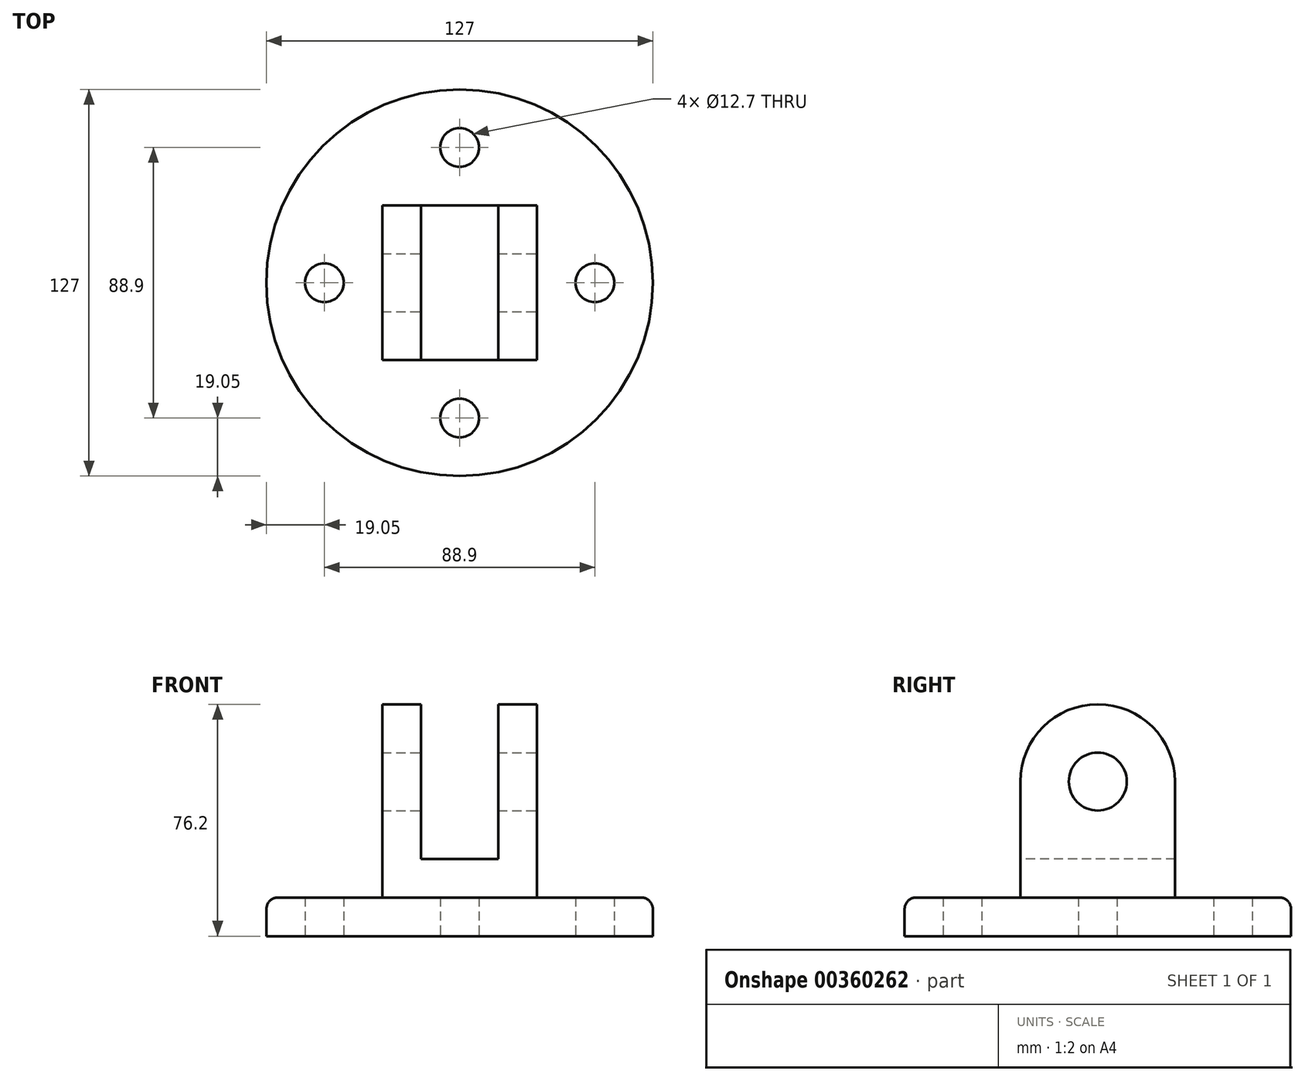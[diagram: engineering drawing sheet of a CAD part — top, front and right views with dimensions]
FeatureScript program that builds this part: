
annotation { "Feature Type Name" : "Feature", "Feature Type Description" : "" }
export const myFeature = defineFeature(function(context is Context, id is Id, definition is map)
    precondition{}
    {
        {
            var Q0;
            Q0=qCreatedBy(makeId("Top.planeOp"),FACE);
            var sketch = newSketch(context, id + "F0", { "sketchPlane" : qUnion([Q0])});
            skCircle(sketch, "E0", {"center": v(0, 0) * mm, "radius": 63.5 * mm});
            skCircle(sketch, "E1", {"center": v(0, 44.45) * mm, "radius": 6.35 * mm});
            skCircle(sketch, "E2.1.0", {"center": v(44.45, 0) * mm, "radius": 6.35 * mm});
            skCircle(sketch, "E2.2.0", {"center": v(0, -44.45) * mm, "radius": 6.35 * mm});
            skCircle(sketch, "E2.3.0", {"center": v(-44.45, 0) * mm, "radius": 6.35 * mm});
            skLineSegment(sketch, "E2.anchor1", {"start": v(0, 0) * mm, "end": v(0, 44.45) * mm, "construction": true});
            skLineSegment(sketch, "E2.anchor2", {"start": v(0, 0) * mm, "end": v(-44.45, 0) * mm, "construction": true});
            skSolve(sketch);
        }
        {
            var Q0;
            Q0=makeQuery(id+"F0.imprint","IMPRINT",FACE,{"disambiguationData":[TD([[makeQuery(id+"F0.imprint","IMPRINT",EDGE,{"derivedFrom":sQuery(id+"F0.wireOp",EDGE,"E0")}),1.0]])]});
            extrude(context, id + "F1", {"entities" : qUnion([Q0]), "endBound" : BoundingType.SYMMETRIC, "depth" : 12.7 * mm});
        }
        {
            var Q0;
            Q0=makeQuery(id+"F1.opExtrude","CAP_FACE",FACE,{"disambiguationData":[OSD([sQuery(id+"F0.wireOp",EDGE,"E0"),sQuery(id+"F0.wireOp",EDGE,"E1"),sQuery(id+"F0.wireOp",EDGE,"E2.1.0"),sQuery(id+"F0.wireOp",EDGE,"E2.2.0"),sQuery(id+"F0.wireOp",EDGE,"E2.3.0")])],"isStart":false});
            var sketch = newSketch(context, id + "F2", { "sketchPlane" : qUnion([Q0])});
            skLineSegment(sketch, "E3.bottom", {"start": v(25.4, -25.4) * mm, "end": v(-25.4, -25.4) * mm});
            skLineSegment(sketch, "E3.top", {"start": v(25.4, 25.4) * mm, "end": v(-25.4, 25.4) * mm});
            skLineSegment(sketch, "E3.left", {"start": v(25.4, -25.4) * mm, "end": v(25.4, 25.4) * mm});
            skLineSegment(sketch, "E3.right", {"start": v(-25.4, -25.4) * mm, "end": v(-25.4, 25.4) * mm});
            skPoint(sketch, "E3.middle", {"position": v(0, 0) * mm});
            skSolve(sketch);
        }
        {
            var Q0;
            Q0=makeQuery(id+"F2.imprint","IMPRINT",FACE,{"disambiguationData":[TD([[makeQuery(id+"F2.imprint","IMPRINT",EDGE,{"derivedFrom":sQuery(id+"F2.wireOp",EDGE,"E3.bottom")}),-1.0]])]});
            extrude(context, id + "F3", {"entities" : qUnion([Q0]), "operationType" : NewBodyOperationType.ADD, "depth" : 38.1 * mm});
        }
        {
            var Q0;
            Q0=makeQuery(id+"F3.opExtrude","SWEPT_FACE",FACE,{"disambiguationData":[OSD([sQuery(id+"F2.wireOp",EDGE,"E3.left")])]});
            var sketch = newSketch(context, id + "F4", { "sketchPlane" : qUnion([Q0])});
            skArc(sketch, "E4", {"start": v(25.4, 44.45) * mm, "mid": v(0, 69.85) * mm, "end": v(-25.4, 44.45) * mm});
            skSolve(sketch);
        }
        {
            var Q0;
            Q0=makeQuery(id+"F4.imprint","IMPRINT",FACE,{"disambiguationData":[TD([[makeQuery(id+"F4.imprint","IMPRINT",EDGE,{"derivedFrom":sQuery(id+"F4.wireOp",EDGE,"E4")}),1.0]])]});
            var Q1;
            Q1=makeQuery(id+"F3.opExtrude","SWEPT_FACE",FACE,{"disambiguationData":[OSD([sQuery(id+"F2.wireOp",EDGE,"E3.right")])]});
            extrude(context, id + "F5", {"entities" : qUnion([Q0]), "operationType" : NewBodyOperationType.ADD, "endBound" : BoundingType.UP_TO_SURFACE, "oppositeDirection" : true, "endBoundEntityFace" : qUnion([Q1]), "depth" : 25.4 * mm});
        }
        {
            var Q0;
            Q0=makeQuery(id+"F3.opExtrude","SWEPT_FACE",FACE,{"disambiguationData":[OSD([sQuery(id+"F2.wireOp",EDGE,"E3.bottom")])]});
            var sketch = newSketch(context, id + "F6", { "sketchPlane" : qUnion([Q0])});
            skLineSegment(sketch, "E5.bottom", {"start": v(-12.7, 69.85) * mm, "end": v(12.7, 69.85) * mm});
            skLineSegment(sketch, "E5.top", {"start": v(-12.7, 19.05) * mm, "end": v(12.7, 19.05) * mm});
            skLineSegment(sketch, "E5.left", {"start": v(-12.7, 69.85) * mm, "end": v(-12.7, 19.05) * mm});
            skLineSegment(sketch, "E5.right", {"start": v(12.7, 69.85) * mm, "end": v(12.7, 19.05) * mm});
            skLineSegment(sketch, "E6", {"start": v(0, 0) * mm, "end": v(0, 73.44) * mm, "construction": true});
            skPoint(sketch, "E6.endSnap0", {"position": v(0, 6.35) * mm});
            skLineSegment(sketch, "E7", {"start": v(-25.4, 69.85) * mm, "end": v(25.4, 69.85) * mm});
            skSolve(sketch);
        }
        {
            var Q0;
            {var subQ0=sQuery(id+"F6.wireOp",EDGE,"E5.top");Q0=makeQuery(id+"F6.imprint","IMPRINT",FACE,{"disambiguationData":[TD([[makeQuery(id+"F6.imprint","IMPRINT",EDGE,{"derivedFrom":subQ0}),1.0]])]});}
            var Q1;
            {var subQ0=sQuery(id+"F6.wireOp",EDGE,"E5.bottom");Q1=makeQuery(id+"F6.imprint","IMPRINT",FACE,{"disambiguationData":[TD([[makeQuery(id+"F6.imprint","IMPRINT",EDGE,{"derivedFrom":subQ0}),-1.0]])]});}
            var Q2;
            {var subQ0=sQuery(id+"F6.wireOp",EDGE,"E7");var subQ1=sQuery(id+"F6.wireOp",EDGE,"E5.left");var subQ2=makeQuery(id+"F6.imprint","INTERSECT",VERTEX,{"derivedFrom":[subQ1,subQ0]});Q2=makeQuery(id+"F6.imprint","IMPRINT",FACE,{"disambiguationData":[TD([[makeQuery(id+"F6.imprint","IMPRINT",EDGE,{"disambiguationData":[TD([[subQ2,-1.0]])],"derivedFrom":subQ0}),-1.0]])]});}
            extrude(context, id + "F7", {"entities" : qUnion([Q0, Q1, Q2]), "operationType" : NewBodyOperationType.REMOVE, "endBound" : BoundingType.THROUGH_ALL, "oppositeDirection" : true, "depth" : 25.4 * mm});
        }
        {
            var Q0;
            {var subQ0=sQuery(id+"F2.wireOp",EDGE,"E3.left");Q0=makeQuery(id+"F5.boolean.opBoolean","MERGE",FACE,{"derivedFrom":[makeQuery(id+"F3.opExtrude","SWEPT_FACE",FACE,{"disambiguationData":[OSD([subQ0])]}),makeQuery(id+"F5.opExtrude","CAP_FACE",FACE,{"disambiguationData":[OSD([subQ0,sQuery(id+"F4.wireOp",EDGE,"E4")])],"isStart":true})]});}
            var sketch = newSketch(context, id + "F8", { "sketchPlane" : qUnion([Q0])});
            skCircle(sketch, "E8", {"center": v(0, 44.45) * mm, "radius": 9.53 * mm});
            skSolve(sketch);
        }
        {
            var Q0;
            Q0=makeQuery(id+"F8.imprint","IMPRINT",FACE,{"disambiguationData":[TD([[makeQuery(id+"F8.imprint","IMPRINT",EDGE,{"derivedFrom":sQuery(id+"F8.wireOp",EDGE,"E8")}),1.0]])]});
            extrude(context, id + "F9", {"entities" : qUnion([Q0]), "operationType" : NewBodyOperationType.REMOVE, "endBound" : BoundingType.THROUGH_ALL, "oppositeDirection" : true, "depth" : 25.4 * mm});
        }
        {
            var Q0;
            Q0=makeQuery(id+"F1.opExtrude","CAP_EDGE",EDGE,{"disambiguationData":[OSD([sQuery(id+"F0.wireOp",EDGE,"E0")])],"isStart":false});
            var Q1;
            Q1=makeQuery(id+"F3.opExtrude","CAP_EDGE",EDGE,{"disambiguationData":[OSD([sQuery(id+"F2.wireOp",EDGE,"E3.left")])],"isStart":true});
            var Q2;
            Q2=makeQuery(id+"F3.opExtrude","CAP_EDGE",EDGE,{"disambiguationData":[OSD([sQuery(id+"F2.wireOp",EDGE,"E3.bottom")])],"isStart":true});
            var Q3;
            Q3=makeQuery(id+"F3.opExtrude","CAP_EDGE",EDGE,{"disambiguationData":[OSD([sQuery(id+"F2.wireOp",EDGE,"E3.right")])],"isStart":true});
            var Q4;
            Q4=makeQuery(id+"F3.opExtrude","CAP_EDGE",EDGE,{"disambiguationData":[OSD([sQuery(id+"F2.wireOp",EDGE,"E3.top")])],"isStart":true});
            fillet(context, id + "F10", {"entities" : qUnion([Q0, Q1, Q2, Q3, Q4]), "radius" : 3.8 * mm, "tangentPropagation" : true, "allowEdgeOverflow" : false});
        }
    });
